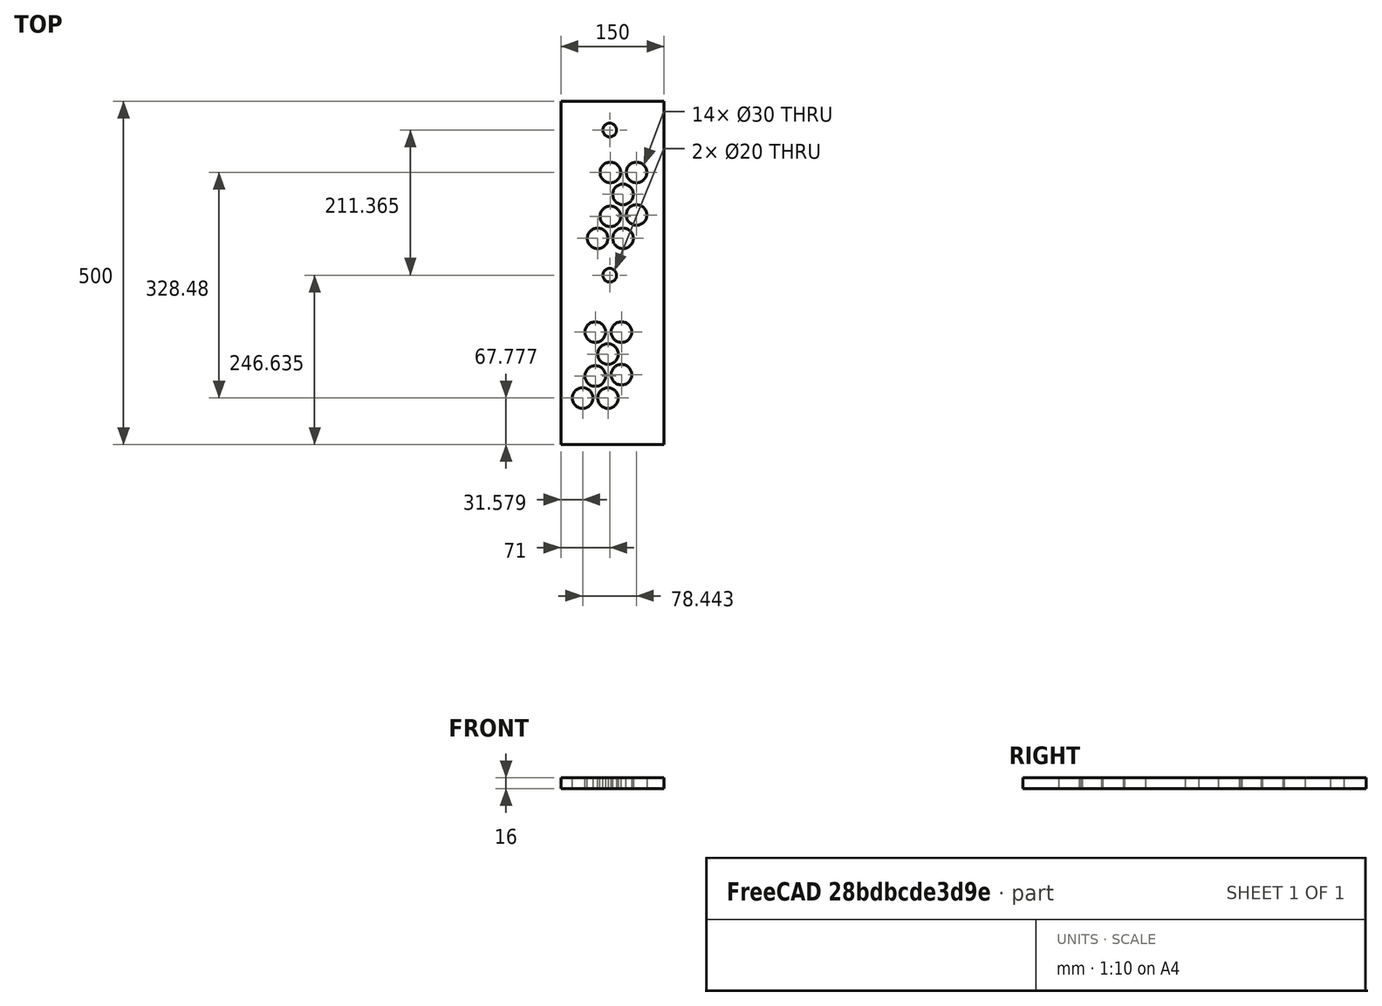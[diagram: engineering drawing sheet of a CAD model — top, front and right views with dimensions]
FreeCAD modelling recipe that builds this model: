
FCSTD DOCUMENT  (FreeCAD 0.18R14555 (Git shallow))
Label: 1001_keyboard_500_16_Duo
License: All rights reserved
LicenseURL: http://en.wikipedia.org/wiki/All_rights_reserved
objects: Sketcher::SketchObject×2, PartDesign::Pad×1, PartDesign::Pocket×1, PartDesign::Body×1, TechDraw::DrawSVGTemplate×1, TechDraw::DrawViewPart×1, TechDraw::DrawViewDimension×1, TechDraw::DrawPage×1, Spreadsheet::Sheet×1
note: 7 computed .brp shape members not serialized (recipe doc carries the construction recipe); baked Part::Feature solids carry a one-line shape summary decoded from their .brp

FEATURE [Sketcher::SketchObject] Sketch
  MapMode = 5
  Support = -> [XY_Plane]
  expr: Constraints[6] = xls.k_d
  expr: Constraints[5] = xls.k_w
  sketch-geometry (5):
    g0: LineSegment StartX=0 StartY=500 StartZ=0 EndX=150 EndY=500 EndZ=0
    g1: LineSegment StartX=150 StartY=500 StartZ=0 EndX=150 EndY=0 EndZ=0
    g2: LineSegment StartX=150 StartY=0 StartZ=0 EndX=0 EndY=0 EndZ=0
    g3: LineSegment StartX=0 StartY=0 StartZ=0 EndX=0 EndY=250 EndZ=0
    g4: LineSegment StartX=0 StartY=250 StartZ=0 EndX=0 EndY=500 EndZ=0
  constraints (14):
    c: Coincident(g0,g1)
    c: Coincident(g1,g2)
    c: Horizontal(g0)
    c: Horizontal(g2)
    c: Vertical(g1)
    c: DistanceY(g1,g1) = 500
    c: DistanceX(g0,g0) = 150
    c: Coincident(g3,g2)
    c: Coincident(g4,g0)
    c: Equal(g3,g4)
    c: Vertical(g4)
    c: Vertical(g3)
    c: Coincident(g3,g4)
    c: Coincident(g2,g-1)
FEATURE [PartDesign::Pad] Pad
  Length = 16
  Length2 = 100
  Profile = -> Sketch
  Type = 0
  expr: Length = xls.k_t_0
FEATURE [Sketcher::SketchObject] Sketch001
  ExternalGeometry = -> [Pad]
  MapMode = 5
  Placement = pos=(0,0,16) rot=(0,0,1;0rad)
  Support = -> [Pad]
  sketch-geometry (66):
    g0: LineSegment [constr] StartX=68.5295 StartY=67.7773 StartZ=0 EndX=68.5295 EndY=99.7773 EndZ=0
    g1: LineSegment [constr] StartX=68.5295 StartY=99.7773 StartZ=0 EndX=68.5295 EndY=131.777 EndZ=0
    g2: LineSegment [constr] StartX=68.5295 StartY=131.777 StartZ=0 EndX=68.5295 EndY=163.777 EndZ=0
    g3: LineSegment [constr] StartX=68.5295 StartY=131.777 StartZ=0 EndX=50.0543 EndY=163.777 EndZ=0
    g4: LineSegment [constr] StartX=68.5295 StartY=131.777 StartZ=0 EndX=50.0543 EndY=99.7773 EndZ=0
    g5: LineSegment [constr] StartX=50.0543 StartY=99.7773 StartZ=0 EndX=31.5791 EndY=67.7773 EndZ=0
    g6: LineSegment [constr] StartX=31.5791 StartY=67.7773 StartZ=0 EndX=68.5295 EndY=67.7773 EndZ=0
    g7: LineSegment [constr] StartX=50.0543 StartY=99.7773 StartZ=0 EndX=68.5295 EndY=99.7773 EndZ=0
    g8: LineSegment [constr] StartX=50.0543 StartY=163.777 StartZ=0 EndX=68.5295 EndY=163.777 EndZ=0
    g9: Circle CenterX=31.5791 CenterY=67.7773 CenterZ=0 NormalX=0 NormalY=0 NormalZ=1 AngleXU=0 Radius=15
    g10: Circle CenterX=50.0543 CenterY=99.7773 CenterZ=0 NormalX=0 NormalY=0 NormalZ=1 AngleXU=0 Radius=15
    g11: Circle CenterX=68.5295 CenterY=131.777 CenterZ=0 NormalX=0 NormalY=0 NormalZ=1 AngleXU=0 Radius=15
    g12: Circle CenterX=50.0543 CenterY=163.777 CenterZ=0 NormalX=0 NormalY=0 NormalZ=1 AngleXU=0 Radius=15
    g13: Circle CenterX=71 CenterY=246.635 CenterZ=0 NormalX=0 NormalY=0 NormalZ=1 AngleXU=0 Radius=10
    g14: LineSegment [constr] StartX=0 StartY=12 StartZ=0 EndX=136.275 EndY=12 EndZ=0
    g15: LineSegment [constr] StartX=136.275 StartY=12 StartZ=0 EndX=136.275 EndY=0 EndZ=0
    g16: LineSegment [constr] StartX=136.275 StartY=0 StartZ=0 EndX=0 EndY=0 EndZ=0
    g17: LineSegment [constr] StartX=0 StartY=0 StartZ=0 EndX=0 EndY=12 EndZ=0
    g18: LineSegment [constr] StartX=30 StartY=276.635 StartZ=0 EndX=112 EndY=276.635 EndZ=0
    g19: LineSegment [constr] StartX=112 StartY=276.635 StartZ=0 EndX=112 EndY=216.635 EndZ=0
    g20: LineSegment [constr] StartX=112 StartY=216.635 StartZ=0 EndX=30 EndY=216.635 EndZ=0
    g21: LineSegment [constr] StartX=30 StartY=216.635 StartZ=0 EndX=30 EndY=276.635 EndZ=0
    g22: LineSegment [constr] StartX=30 StartY=216.635 StartZ=0 EndX=71 EndY=246.635 EndZ=0
    g23: LineSegment [constr] StartX=71 StartY=246.635 StartZ=0 EndX=30 EndY=276.635 EndZ=0
    g24: LineSegment [constr] StartX=71 StartY=246.635 StartZ=0 EndX=112 EndY=216.635 EndZ=0
    g25: Circle CenterX=68.5295 CenterY=67.7773 CenterZ=0 NormalX=0 NormalY=0 NormalZ=1 AngleXU=0 Radius=15
    g26: Circle CenterX=88.1594 CenterY=101.777 CenterZ=0 NormalX=0 NormalY=0 NormalZ=1 AngleXU=0 Radius=15
    g27: LineSegment [constr] StartX=68.5295 StartY=67.7773 StartZ=0 EndX=88.1594 EndY=101.777 EndZ=0
    g28: LineSegment [constr] StartX=88.1594 StartY=101.777 StartZ=0 EndX=88.1594 EndY=163.777 EndZ=0
    g29: LineSegment [constr] StartX=88.1594 StartY=163.777 StartZ=0 EndX=68.5295 EndY=163.777 EndZ=0
    g30: Circle CenterX=88.1594 CenterY=163.777 CenterZ=0 NormalX=0 NormalY=0 NormalZ=1 AngleXU=0 Radius=15
    g31: LineSegment [constr] StartX=90.3919 StartY=300.257 StartZ=0 EndX=90.3919 EndY=332.257 EndZ=0
    g32: LineSegment [constr] StartX=90.3919 StartY=332.257 StartZ=0 EndX=90.3919 EndY=364.257 EndZ=0
    g33: LineSegment [constr] StartX=90.3919 StartY=364.257 StartZ=0 EndX=90.3919 EndY=396.257 EndZ=0
    g34: LineSegment [constr] StartX=90.3919 StartY=364.257 StartZ=0 EndX=71.9167 EndY=396.257 EndZ=0
    g35: LineSegment [constr] StartX=90.3919 StartY=364.257 StartZ=0 EndX=71.9167 EndY=332.257 EndZ=0
    g36: LineSegment [constr] StartX=71.9167 StartY=332.257 StartZ=0 EndX=53.4415 EndY=300.257 EndZ=0
    g37: LineSegment [constr] StartX=53.4415 StartY=300.257 StartZ=0 EndX=90.3919 EndY=300.257 EndZ=0
    g38: LineSegment [constr] StartX=71.9167 StartY=332.257 StartZ=0 EndX=90.3919 EndY=332.257 EndZ=0
    g39: LineSegment [constr] StartX=71.9167 StartY=396.257 StartZ=0 EndX=90.3919 EndY=396.257 EndZ=0
    g40: Circle CenterX=53.4415 CenterY=300.257 CenterZ=0 NormalX=0 NormalY=0 NormalZ=1 AngleXU=0 Radius=15
    g41: Circle CenterX=71.9167 CenterY=332.257 CenterZ=0 NormalX=0 NormalY=0 NormalZ=1 AngleXU=0 Radius=15
    g42: Circle CenterX=90.3919 CenterY=364.257 CenterZ=0 NormalX=0 NormalY=0 NormalZ=1 AngleXU=0 Radius=15
    g43: Circle CenterX=71.9167 CenterY=396.257 CenterZ=0 NormalX=0 NormalY=0 NormalZ=1 AngleXU=0 Radius=15
    g44: Circle CenterX=71 CenterY=458 CenterZ=0 NormalX=0 NormalY=0 NormalZ=1 AngleXU=0 Radius=10
    g45: LineSegment [constr] StartX=30 StartY=488 StartZ=0 EndX=112 EndY=488 EndZ=0
    g46: LineSegment [constr] StartX=112 StartY=488 StartZ=0 EndX=112 EndY=428 EndZ=0
    g47: LineSegment [constr] StartX=112 StartY=428 StartZ=0 EndX=30 EndY=428 EndZ=0
    g48: LineSegment [constr] StartX=30 StartY=428 StartZ=0 EndX=30 EndY=488 EndZ=0
    g49: LineSegment [constr] StartX=30 StartY=428 StartZ=0 EndX=71 EndY=458 EndZ=0
    g50: LineSegment [constr] StartX=71 StartY=458 StartZ=0 EndX=30 EndY=488 EndZ=0
    g51: LineSegment [constr] StartX=71 StartY=458 StartZ=0 EndX=112 EndY=428 EndZ=0
    g52: Circle CenterX=90.3919 CenterY=300.257 CenterZ=0 NormalX=0 NormalY=0 NormalZ=1 AngleXU=0 Radius=15
    g53: Circle CenterX=110.022 CenterY=334.257 CenterZ=0 NormalX=0 NormalY=0 NormalZ=1 AngleXU=0 Radius=15
    g54: LineSegment [constr] StartX=90.3919 StartY=300.257 StartZ=0 EndX=110.022 EndY=334.257 EndZ=0
    g55: LineSegment [constr] StartX=110.022 StartY=334.257 StartZ=0 EndX=110.022 EndY=396.257 EndZ=0
    g56: LineSegment [constr] StartX=110.022 StartY=396.257 StartZ=0 EndX=90.3919 EndY=396.257 EndZ=0
    g57: Circle CenterX=110.022 CenterY=396.257 CenterZ=0 NormalX=0 NormalY=0 NormalZ=1 AngleXU=0 Radius=15
    g58: LineSegment [constr] StartX=112 StartY=276.635 StartZ=0 EndX=168.795 EndY=276.635 EndZ=0
    g59: LineSegment [constr] StartX=168.795 StartY=276.635 StartZ=0 EndX=168.795 EndY=488 EndZ=0
    g60: LineSegment [constr] StartX=112 StartY=488 StartZ=0 EndX=168.795 EndY=488 EndZ=0
    g61: LineSegment [constr] StartX=150 StartY=500 StartZ=0 EndX=169.192 EndY=500 EndZ=0
    g62: LineSegment [constr] StartX=169.192 StartY=500 StartZ=0 EndX=168.795 EndY=488 EndZ=0
    g63: LineSegment [constr] StartX=30 StartY=276.635 StartZ=0 EndX=30 EndY=428 EndZ=0
    g64: GeomPoint X=112 Y=276.635 Z=0
    g65: LineSegment [constr] StartX=30 StartY=488 StartZ=0 EndX=0 EndY=488 EndZ=0
  constraints (166):
    c: Vertical(g0)
    c: Coincident(g2,g1)
    c: Vertical(g2)
    c: Vertical(g1)
    c: Coincident(g0,g1)
    c: Equal(g0,g1)
    c: Equal(g1,g2)
    c: DistanceY(g0,g0) = 32
    c: Coincident(g3,g1)
    c: Coincident(g4,g1)
    c: Coincident(g5,g4)
    c: Coincident(g6,g5)
    c: Coincident(g6,g0)
    c: Horizontal(g6)
    c: Coincident(g8,g3)
    c: Coincident(g8,g2)
    c: Horizontal(g8)
    c: Parallel(g4,g5)
    c: Coincident(g7,g4)
    c: Horizontal(g7)
    c: Coincident(g7,g0)
    c: Equal(g7,g8)
    c: Angle(g4,g1) = 0.523599
    c: Equal(g0,g1)
    c: Equal(g1,g2)
    c: Equal(g7,g8)
    c: Coincident(g9,g5)
    c: Coincident(g10,g4)
    c: Coincident(g11,g1)
    c: Coincident(g12,g3)
    c: Equal(g12,g11)
    c: Equal(g11,g10)
    c: Equal(g10,g9)
    c: Radius(g13) = 10
    c: Radius(g12) = 15
    c: Coincident(g14,g15)
    c: Coincident(g15,g16)
    c: Coincident(g16,g17)
    c: Coincident(g17,g14)
    c: Horizontal(g14)
    c: Horizontal(g16)
    c: Vertical(g15)
    c: Vertical(g17)
    c: DistanceY(g17,g17) = 12
    c: Coincident(g18,g19)
    c: Coincident(g19,g20)
    c: Coincident(g20,g21)
    c: Coincident(g21,g18)
    c: Horizontal(g18)
    c: Horizontal(g20)
    c: Vertical(g19)
    c: Vertical(g21)
    c: PointOnObject(g16,g-2)
    c: PointOnObject(g16,g-3)
    c: Coincident(g22,g20)
    c: Coincident(g23,g22)
    c: Coincident(g23,g18)
    c: Coincident(g24,g22)
    c: Coincident(g24,g19)
    c: Parallel(g24,g23)
    c: Equal(g24,g23)
    c: DistanceY(g21,g21) = 60
    c: DistanceX(g18,g18) = 82
    c: Coincident(g13,g22)
    c: Equal(g26,g25)
    c: Radius(g25) = 15
    c: Coincident(g27,g25)
    c: Coincident(g27,g26)
    c: DistanceY(g27,g27) = 34
    c: Angle(g27,g25) = 0.523599
    c: Coincident(g25,g0)
    c: Parallel(g27,g5)
    c: Coincident(g28,g26)
    c: Vertical(g28)
    c: Coincident(g29,g28)
    c: Coincident(g29,g2)
    c: Horizontal(g29)
    c: Coincident(g30,g28)
    c: Equal(g30,g12)
    c: Vertical(g31)
    c: Coincident(g33,g32)
    c: Vertical(g33)
    c: Vertical(g32)
    c: Coincident(g31,g32)
    c: Equal(g31,g32)
    c: Equal(g32,g33)
    c: Equal(g0,g31) = 32
    c: Coincident(g34,g32)
    c: Coincident(g35,g32)
    c: Coincident(g36,g35)
    c: Coincident(g37,g36)
    c: Coincident(g37,g31)
    c: Horizontal(g37)
    c: Coincident(g39,g34)
    c: Coincident(g39,g33)
    c: Horizontal(g39)
    c: Parallel(g35,g36)
    c: Coincident(g38,g35)
    c: Horizontal(g38)
    c: Coincident(g38,g31)
    c: Equal(g38,g39)
    c: Angle(g35,g32) = 0.523599
    c: Equal(g31,g32)
    c: Equal(g32,g33)
    c: Equal(g38,g39)
    c: Coincident(g40,g36)
    c: Coincident(g41,g35)
    c: Coincident(g42,g32)
    c: Coincident(g43,g34)
    c: Equal(g43,g42)
    c: Equal(g42,g41)
    c: Equal(g41,g40)
    c: Equal(g13,g44) = 10
    c: Equal(g12,g43) = 15
    c: Coincident(g45,g46)
    c: Coincident(g46,g47)
    c: Coincident(g47,g48)
    c: Coincident(g48,g45)
    c: Horizontal(g45)
    c: Horizontal(g47)
    c: Vertical(g46)
    c: Vertical(g48)
    c: Coincident(g49,g47)
    c: Coincident(g50,g49)
    c: Coincident(g50,g45)
    c: Coincident(g51,g49)
    c: Coincident(g51,g46)
    c: Parallel(g51,g50)
    c: Equal(g51,g50)
    c: Equal(g21,g48) = 40
    c: Equal(g18,g45) = 82
    c: Coincident(g44,g49)
    c: Equal(g53,g52)
    c: Equal(g25,g52) = 15
    c: Coincident(g54,g52)
    c: Coincident(g54,g53)
    c: Equal(g27,g54) = 34
    c: Angle(g54,g52) = 0.523599
    c: Coincident(g52,g31)
    c: Parallel(g54,g36)
    c: Coincident(g55,g53)
    c: Vertical(g55)
    c: Coincident(g56,g55)
    c: Coincident(g56,g33)
    c: Horizontal(g56)
    c: Coincident(g57,g55)
    c: Equal(g57,g43)
    c: Coincident(g60,g45)
    c: Coincident(g60,g59)
    c: Horizontal(g60)
    c: Coincident(g61,g-5)
    c: Horizontal(g61)
    c: Coincident(g62,g61)
    c: Coincident(g62,g59)
    c: DistanceY(g62,g62) = 12
    c: Coincident(g63,g18)
    c: Coincident(g63,g47)
    c: Vertical(g63)
    c: Coincident(g64,g58)
    c: Coincident(g18,g64)
    c: Coincident(g65,g45)
    c: PointOnObject(g65,g-2)
    c: Horizontal(g65)
    c: DistanceX(g65,g65) = 30
    c: Coincident(g58,g59)
    c: Horizontal(g58)
FEATURE [PartDesign::Pocket] Pocket
  BaseFeature = -> Pad
  Length = 5
  Length2 = 100
  Profile = -> Sketch001
  Type = 1
FEATURE [PartDesign::Body] Body
  Group = -> [Sketch,Pad,Sketch001,Pocket]
  Origin = -> Origin
  Tip = -> Pocket
FEATURE [TechDraw::DrawSVGTemplate] Template
  EditableTexts = AuthorName=AUTHOR NAME; CheckDate=CHECK DATE; CreationDate=CREATION DATE; DrawingNumber=NUMBER; FC-Scale=SCALE; FC-Title=TITLE; SheetNumber=SHEET; Subtitle=SUBTITLE; SupervisorName=SUPERVISOR NAME; Weight=WEIGHT
  Height = 297
  Orientation = 1
  Width = 420
FEATURE [TechDraw::DrawViewPart] View
  CoarseView = false
  Direction = (0,0,1)
  Focus = 100
  HardHidden = false
  IsoCount = 0
  IsoHidden = false
  IsoVisible = false
  LockPosition = false
  Perspective = false
  Rotation = -90
  ScaleType = 0
  SeamHidden = false
  SeamVisible = false
  SmoothHidden = false
  SmoothVisible = false
  Source = -> [Pocket]
  X = 210
  Y = 148.5
FEATURE [TechDraw::DrawViewDimension] Dimension
  Arbitrary = false
  FormatSpec = %.2f
  LockPosition = false
  MeasureType = 1
  OverTolerance = 0
  References2D = -> [View]
  Rotation = 0
  ScaleType = 0
  Type = 1
  UnderTolerance = 0
  X = 5.19444
  Y = 91.6667
FEATURE [TechDraw::DrawPage] Page
  KeepUpdated = true
  ProjectionType = 0
  Template = -> Template
  Views = -> [View,Dimension]
FEATURE [Spreadsheet::Sheet] Spreadsheet  label="xls"
  cells = B3=KEABOPARD; B4=Thickness; C4=k_t_0; D4(k_t_0)=16; E4=mm; F4=Note:; G4=Plexi is 3mm; B5=Width; C5=k_w; D5(k_w)=500; E5=mm; B6=Deapth; C6=k_d; D6(k_d)=150; E6=mm
